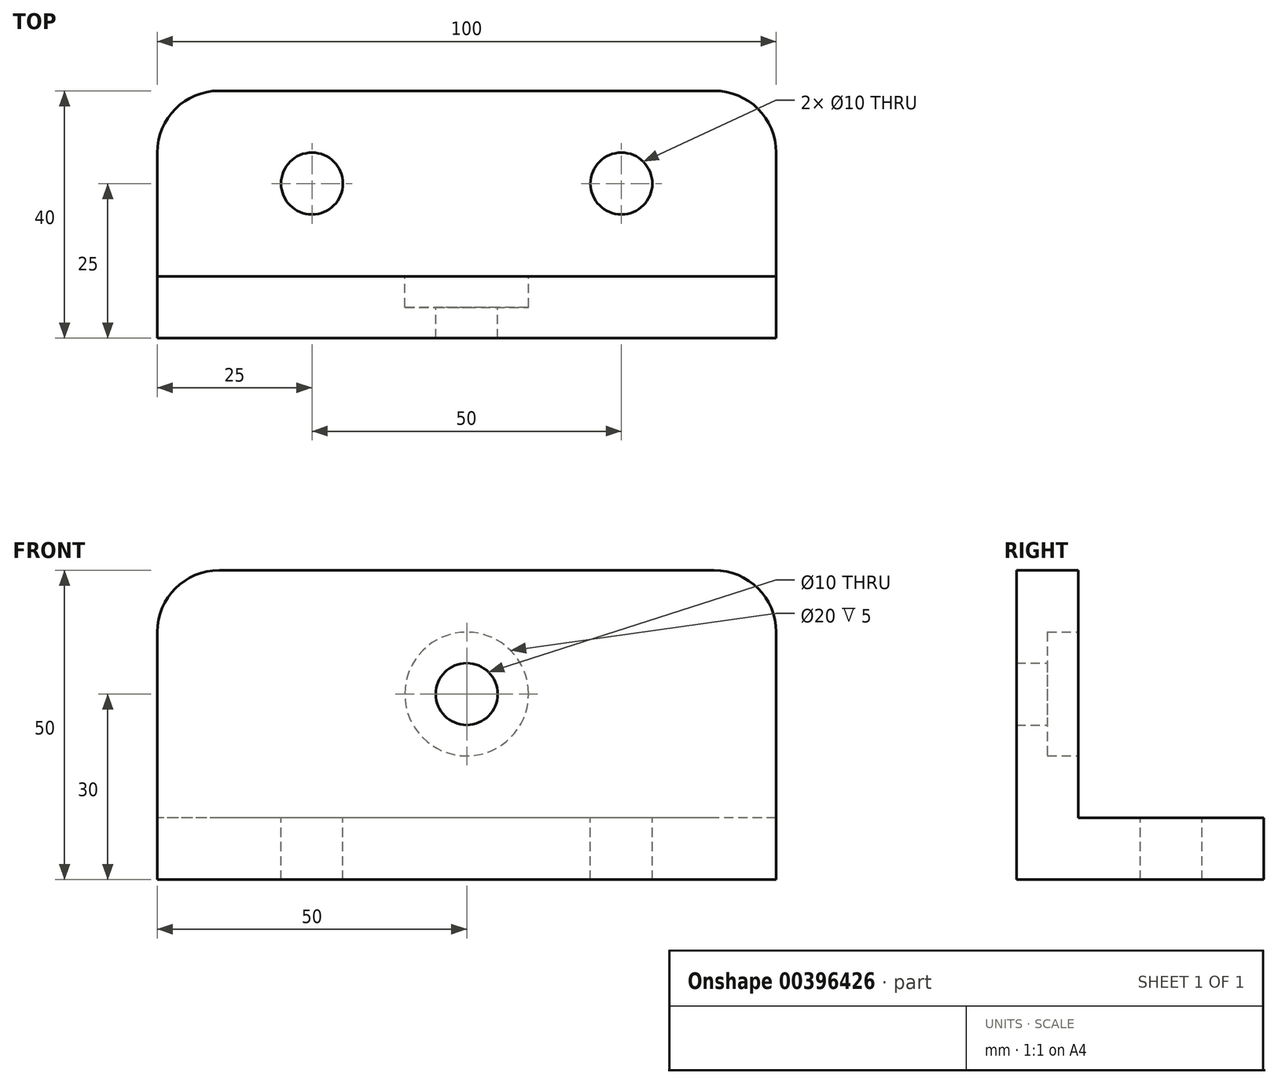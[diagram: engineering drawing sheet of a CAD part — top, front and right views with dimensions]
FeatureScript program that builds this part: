
annotation { "Feature Type Name" : "Feature", "Feature Type Description" : "" }
export const myFeature = defineFeature(function(context is Context, id is Id, definition is map)
    precondition{}
    {
        {
            var Q0;
            Q0=qCreatedBy(makeId("Front.planeOp"),FACE);
            var sketch = newSketch(context, id + "F0", { "sketchPlane" : qUnion([Q0])});
            skLineSegment(sketch, "E0", {"start": v(-50, 40) * mm, "end": v(50, 40) * mm});
            skLineSegment(sketch, "E1", {"start": v(50, 40) * mm, "end": v(50, 0) * mm});
            skLineSegment(sketch, "E2", {"start": v(50, 0) * mm, "end": v(-50, 0) * mm});
            skLineSegment(sketch, "E3", {"start": v(-50, 0) * mm, "end": v(-50, 40) * mm});
            skSolve(sketch);
        }
        {
            var Q0;
            Q0=makeQuery(id+"F0.imprint","IMPRINT",FACE,{"disambiguationData":[TD([[makeQuery(id+"F0.imprint","IMPRINT",EDGE,{"derivedFrom":sQuery(id+"F0.wireOp",EDGE,"E0")}),-1.0]])]});
            extrude(context, id + "F1", {"entities" : qUnion([Q0]), "endBound" : BoundingType.SYMMETRIC, "depth" : 10 * mm});
        }
        {
            var Q0;
            Q0=makeQuery(id+"F1.opExtrude","SWEPT_EDGE",EDGE,{"disambiguationData":[OSD([sQuery(id+"F0.wireOp",EDGE,"E0"),sQuery(id+"F0.wireOp",EDGE,"E3")])]});
            var Q1;
            Q1=makeQuery(id+"F1.opExtrude","SWEPT_EDGE",EDGE,{"disambiguationData":[OSD([sQuery(id+"F0.wireOp",EDGE,"E0"),sQuery(id+"F0.wireOp",EDGE,"E1")])]});
            fillet(context, id + "F2", {"entities" : qUnion([Q0, Q1]), "radius" : 10 * mm, "tangentPropagation" : true, "allowEdgeOverflow" : false});
        }
        {
            var Q0;
            Q0=qCreatedBy(makeId("Top.planeOp"),FACE);
            var sketch = newSketch(context, id + "F3", { "sketchPlane" : qUnion([Q0])});
            skLineSegment(sketch, "E4", {"start": v(50, -5) * mm, "end": v(50, 35) * mm});
            skLineSegment(sketch, "E5", {"start": v(50, 35) * mm, "end": v(-50, 35) * mm});
            skLineSegment(sketch, "E6", {"start": v(-50, 35) * mm, "end": v(-50, -5) * mm});
            skLineSegment(sketch, "E7", {"start": v(-50, -5) * mm, "end": v(50, -5) * mm});
            skSolve(sketch);
        }
        {
            var Q0;
            Q0=makeQuery(id+"F3.imprint","IMPRINT",FACE,{"disambiguationData":[TD([[makeQuery(id+"F3.imprint","IMPRINT",EDGE,{"derivedFrom":sQuery(id+"F3.wireOp",EDGE,"E4")}),1.0]])]});
            extrude(context, id + "F4", {"entities" : qUnion([Q0]), "operationType" : NewBodyOperationType.ADD, "oppositeDirection" : true, "depth" : 10 * mm});
        }
        {
            var Q0;
            Q0=makeQuery(id+"F4.opExtrude","SWEPT_EDGE",EDGE,{"disambiguationData":[OSD([sQuery(id+"F3.wireOp",EDGE,"E5"),sQuery(id+"F3.wireOp",EDGE,"E6")])]});
            var Q1;
            Q1=makeQuery(id+"F4.opExtrude","SWEPT_EDGE",EDGE,{"disambiguationData":[OSD([sQuery(id+"F3.wireOp",EDGE,"E4"),sQuery(id+"F3.wireOp",EDGE,"E5")])]});
            fillet(context, id + "F5", {"entities" : qUnion([Q0, Q1]), "radius" : 10 * mm, "tangentPropagation" : true, "allowEdgeOverflow" : false});
        }
        {
            var Q0;
            Q0=makeQuery(id+"F4.opExtrude","CAP_FACE",FACE,{"disambiguationData":[OSD([sQuery(id+"F3.wireOp",EDGE,"E4"),sQuery(id+"F3.wireOp",EDGE,"E5"),sQuery(id+"F3.wireOp",EDGE,"E6"),sQuery(id+"F3.wireOp",EDGE,"E7")])],"isStart":true});
            var sketch = newSketch(context, id + "F6", { "sketchPlane" : qUnion([Q0])});
            skCircle(sketch, "E8", {"center": v(-25, 20) * mm, "radius": 5 * mm});
            skCircle(sketch, "E9.MirrorC", {"center": v(25, 20) * mm, "radius": 5 * mm});
            skSolve(sketch);
        }
        {
            var Q0;
            Q0=makeQuery(id+"F1.opExtrude","CAP_FACE",FACE,{"disambiguationData":[OSD([sQuery(id+"F0.wireOp",EDGE,"E0"),sQuery(id+"F0.wireOp",EDGE,"E1"),sQuery(id+"F0.wireOp",EDGE,"E2"),sQuery(id+"F0.wireOp",EDGE,"E3")])],"isStart":true});
            var sketch = newSketch(context, id + "F7", { "sketchPlane" : qUnion([Q0])});
            skCircle(sketch, "E10", {"center": v(0, 20) * mm, "radius": 12.5 * mm});
            skSolve(sketch);
        }
        {
            var Q0;
            Q0=sQuery(id+"F6.wireOp",VERTEX,"E9.MirrorC.center");
            var Q1;
            Q1=sQuery(id+"F6.wireOp",VERTEX,"E8.center");
            var Q2;
            Q2=makeQuery(id+"F1.opExtrude","SWEPT_BODY",BODY,{"disambiguationData":[OSD([sQuery(id+"F0.wireOp",EDGE,"E0"),sQuery(id+"F0.wireOp",EDGE,"E1"),sQuery(id+"F0.wireOp",EDGE,"E2"),sQuery(id+"F0.wireOp",EDGE,"E3")])]});
            hole(context, id + "F8", {"style" : HoleStyle.SIMPLE, "endStyle" : HoleEndStyle.THROUGH, "holeDiameter" : 10 * mm, "isTappedThrough" : true, "tappedDepth" : 12 * mm, "tapClearance" : 3, "startFromSketch" : true, "locations" : qUnion([Q0, Q1]), "scope" : qUnion([Q2])});
        }
        {
            var Q0;
            Q0=sQuery(id+"F7.wireOp",VERTEX,"E10.center");
            var Q1;
            Q1=makeQuery(id+"F1.opExtrude","SWEPT_BODY",BODY,{"disambiguationData":[OSD([sQuery(id+"F0.wireOp",EDGE,"E0"),sQuery(id+"F0.wireOp",EDGE,"E1"),sQuery(id+"F0.wireOp",EDGE,"E2"),sQuery(id+"F0.wireOp",EDGE,"E3")])]});
            hole(context, id + "F9", {"style" : HoleStyle.C_BORE, "endStyle" : HoleEndStyle.THROUGH, "holeDiameter" : 10 * mm, "cBoreDiameter" : 20 * mm, "cBoreDepth" : 5 * mm, "isTappedThrough" : true, "tappedDepth" : 12 * mm, "tapClearance" : 3, "startFromSketch" : true, "locations" : qUnion([Q0]), "scope" : qUnion([Q1])});
        }
    });
